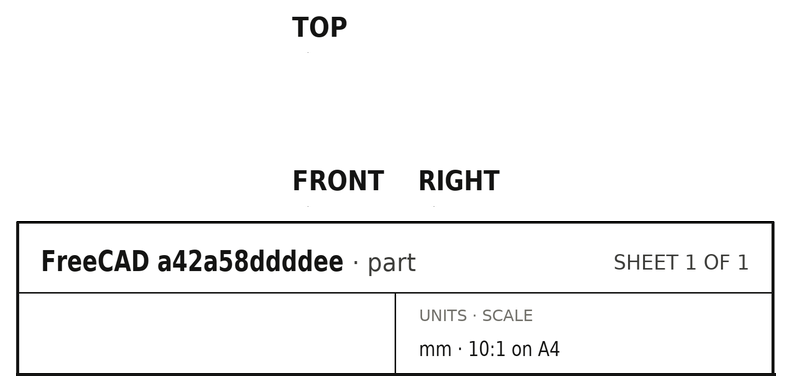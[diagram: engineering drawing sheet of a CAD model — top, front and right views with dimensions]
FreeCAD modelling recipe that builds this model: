
FCSTD DOCUMENT  (FreeCAD 0.21R33694 (Git))
Label: diffPair
License: All rights reserved
LicenseURL: http://en.wikipedia.org/wiki/All_rights_reserved
objects: Part::Part2DObjectPython×23, App::FeaturePython×10, Part::Extrusion×5, Part::Cut×3, Part::FeaturePython×2
note: 33 computed .brp shape members not serialized (recipe doc carries the construction recipe); baked Part::Feature solids carry a one-line shape summary decoded from their .brp

FEATURE [Part::Part2DObjectPython] Wire  # Draft 2D object (typed FeaturePython)
  Area = 0.0014181
  ChamferSize = 0
  Closed = true
  End = (-0.05,0,0)
  FilletRadius = 0
  Length = 0.221006
  MakeFace = true
  Placement = pos=(-0.15,0,0) rot=(0,0,1;0rad)
  Points = (4) [(0,0,0),(0.00545955,0.015,0),(0.0945402,0.015,0),(0.1,-6.12323e-18,0)]
  Start = (-0.15,0,0)
  Subdivisions = 0
FEATURE [Part::Part2DObjectPython] Wire001  # Draft 2D object (typed FeaturePython)
  Area = 0.0014181
  ChamferSize = 0
  Closed = true
  End = (0.15,0,0)
  FilletRadius = 0
  Length = 0.221006
  MakeFace = true
  Placement = pos=(0.05,0,0) rot=(0,0,1;0rad)
  Points = (4) [(0,0,0),(0.00545955,0.015,0),(0.0945402,0.015,0),(0.1,-6.12323e-18,0)]
  Start = (0.05,0,0)
  Subdivisions = 0
FEATURE [Part::Part2DObjectPython] Rectangle  # Draft 2D object (typed FeaturePython)
  Area = 0.13
  ChamferSize = 0
  Columns = 1
  FilletRadius = 0
  Height = 0.1
  Length = 1.3
  MakeFace = true
  Placement = pos=(-0.65,-0.1,0) rot=(0,0,1;0rad)
  Rows = 1
FEATURE [Part::Part2DObjectPython] Rectangle001  # Draft 2D object (typed FeaturePython)
  Area = 0.13
  ChamferSize = 0
  Columns = 1
  FilletRadius = 0
  Height = 0.1
  Length = 1.3
  MakeFace = true
  Placement = pos=(-0.65,0,0) rot=(0,0,1;0rad)
  Rows = 1
FEATURE [Part::Part2DObjectPython] Clone2D  label="Wire (2D)"  # Draft 2D object (typed FeaturePython)
  Fuse = false
  Objects = -> [Wire]
  Placement = pos=(-0.15,0,0) rot=(0,0,1;0rad)
  Scale = (1,1,1)
FEATURE [Part::Part2DObjectPython] Clone2D001  label="Wire001 (2D)"  # Draft 2D object (typed FeaturePython)
  Fuse = false
  Objects = -> [Wire001]
  Placement = pos=(0.05,0,0) rot=(0,0,1;0rad)
  Scale = (1,1,1)
FEATURE [Part::Part2DObjectPython] Clone2D002  label="Rectangle (2D)"  # Draft 2D object (typed FeaturePython)
  Fuse = false
  Objects = -> [Rectangle]
  Placement = pos=(-0.65,-0.1,0) rot=(0,0,1;0rad)
  Scale = (1,1,1)
FEATURE [Part::Part2DObjectPython] Clone2D003  label="Rectangle001 (2D)"  # Draft 2D object (typed FeaturePython)
  Fuse = false
  Objects = -> [Rectangle001]
  Placement = pos=(-0.65,0,0) rot=(0,0,1;0rad)
  Scale = (1,1,1)
FEATURE [Part::Part2DObjectPython] Clone2D004  label="Wire (2D)001"  # Draft 2D object (typed FeaturePython)
  Fuse = false
  Objects = -> [Wire]
  Placement = pos=(-0.15,0,0) rot=(0,0,1;0rad)
  Scale = (1,1,1)
FEATURE [Part::Part2DObjectPython] Clone2D005  label="Wire001 (2D)001"  # Draft 2D object (typed FeaturePython)
  Fuse = false
  Objects = -> [Wire001]
  Placement = pos=(0.05,0,0) rot=(0,0,1;0rad)
  Scale = (1,1,1)
FEATURE [Part::Part2DObjectPython] Clone2D006  label="Rectangle (2D)001"  # Draft 2D object (typed FeaturePython)
  Fuse = false
  Objects = -> [Rectangle]
  Placement = pos=(-0.65,-0.1,0) rot=(0,0,1;0rad)
  Scale = (1,1,1)
FEATURE [Part::Part2DObjectPython] Clone2D007  label="Rectangle001 (2D)001"  # Draft 2D object (typed FeaturePython)
  Fuse = false
  Objects = -> [Rectangle001]
  Placement = pos=(-0.65,0,0) rot=(0,0,1;0rad)
  Scale = (1,1,1)
FEATURE [Part::Extrusion] Extrude004
  Base = -> Clone2D
  Dir = (0,0,1)
  DirMode = 2
  FaceMakerClass = Part::FaceMakerBullseye
  LengthFwd = 2
  LengthRev = 0
  Solid = false
  Symmetric = false
FEATURE [Part::Extrusion] Extrude005
  Base = -> Clone2D001
  Dir = (0,0,1)
  DirMode = 2
  FaceMakerClass = Part::FaceMakerBullseye
  LengthFwd = 2
  LengthRev = 0
  Solid = false
  Symmetric = false
FEATURE [Part::Extrusion] Extrude006
  Base = -> Clone2D002
  Dir = (0,0,1)
  DirMode = 2
  FaceMakerClass = Part::FaceMakerBullseye
  LengthFwd = 2
  LengthRev = 0
  Solid = false
  Symmetric = false
FEATURE [Part::Extrusion] Extrude007
  Base = -> Clone2D003
  Dir = (0,0,1)
  DirMode = 2
  FaceMakerClass = Part::FaceMakerBullseye
  LengthFwd = 2
  LengthRev = 0
  Solid = false
  Symmetric = false
FEATURE [Part::Cut] Cut002
  Base = -> Extrude007
  Tool = -> Extrude004
FEATURE [Part::Cut] Cut003
  Base = -> Cut002
  Tool = -> Extrude005
FEATURE [App::FeaturePython] Text010  label="_Sin(PV){port1}"  # WARN: FeaturePython — macro-defined, semantics opaque (R4)
  Placement = pos=(5.00075,-5.09743,10) rot=(0,0,1;0rad)
  Text = .
FEATURE [App::FeaturePython] Text011  label="_Sout(PV){port2}"  # WARN: FeaturePython — macro-defined, semantics opaque (R4)
  Placement = pos=(5.00075,-5.09743,10) rot=(0,0,1;0rad)
  Text = .
FEATURE [App::FeaturePython] Text012  label="_Lin(1,voltage,in1){v11}"  # WARN: FeaturePython — macro-defined, semantics opaque (R4)
  Placement = pos=(5.00075,-5.09743,10) rot=(0,0,1;0rad)
  Text = .
FEATURE [App::FeaturePython] Text013  label="_Lin(1,current,in1){i11}"  # WARN: FeaturePython — macro-defined, semantics opaque (R4)
  Placement = pos=(5.00075,-5.09743,10) rot=(0,0,1;0rad)
  Text = .
FEATURE [App::FeaturePython] Text014  label="_Lin(2,voltage,in2){v12}"  # WARN: FeaturePython — macro-defined, semantics opaque (R4)
  Placement = pos=(5.00075,-5.09743,10) rot=(0,0,1;0rad)
  Text = .
FEATURE [App::FeaturePython] Text015  label="_Lin(2,current,in2){i12}"  # WARN: FeaturePython — macro-defined, semantics opaque (R4)
  Placement = pos=(5.00075,-5.09743,10) rot=(0,0,1;0rad)
  Text = .
FEATURE [App::FeaturePython] Text016  label="_Lout(3,voltage,out3){v21}"  # WARN: FeaturePython — macro-defined, semantics opaque (R4)
  Placement = pos=(5.00075,-5.09743,10) rot=(0,0,1;0rad)
  Text = .
FEATURE [App::FeaturePython] Text017  label="_Lout(3,current,out3){i21}"  # WARN: FeaturePython — macro-defined, semantics opaque (R4)
  Placement = pos=(5.00075,-5.09743,10) rot=(0,0,1;0rad)
  Text = .
FEATURE [App::FeaturePython] Text018  label="_Lout(4,voltage,out4){v22}"  # WARN: FeaturePython — macro-defined, semantics opaque (R4)
  Placement = pos=(5.00075,-5.09743,10) rot=(0,0,1;0rad)
  Text = .
FEATURE [App::FeaturePython] Text019  label="_Lout(4,current,out4){i22}"  # WARN: FeaturePython — macro-defined, semantics opaque (R4)
  Placement = pos=(5.00075,-5.09743,10) rot=(0,0,1;0rad)
  Text = .
FEATURE [Part::Part2DObjectPython] Wire006  label="_Pi22"  # Draft 2D object (typed FeaturePython)
  Area = 1.4181e-09
  ChamferSize = 0
  Closed = true
  End = (5e-05,-0.0999,4.995)
  FilletRadius = 0
  Length = 0.000221006
  MakeFace = true
  Placement = pos=(0.00015,-0.0999,4.995) rot=(0.707107,0.707107,0;3.14159rad)
  Points = (4) [(0,0,0),(1.5e-05,-5.45983e-06,0),(1.5e-05,-9.45404e-05,0),(0,-0.0001,0)]
  Start = (0.00015,-0.0999,4.995)
  Subdivisions = 0
FEATURE [Part::Part2DObjectPython] Wire007  label="_Pi21"  # Draft 2D object (typed FeaturePython)
  Area = 1.4181e-09
  ChamferSize = 0
  Closed = true
  End = (-0.00015,-0.0999,4.995)
  FilletRadius = 0
  Length = 0.000221006
  MakeFace = true
  Placement = pos=(-5e-05,-0.0999,4.995) rot=(0.707107,0.707107,0;3.14159rad)
  Points = (4) [(0,0,0),(1.5e-05,-5.45983e-06,0),(1.5e-05,-9.45404e-05,0),(0,-0.0001,0)]
  Start = (-5e-05,-0.0999,4.995)
  Subdivisions = 0
FEATURE [Part::Part2DObjectPython] Wire008  label="_Pi11"  # Draft 2D object (typed FeaturePython)
  Area = 1.4181e-09
  ChamferSize = 0
  Closed = true
  End = (-5e-05,-0.0999,4.997)
  FilletRadius = 0
  Length = 0.000221006
  MakeFace = true
  Placement = pos=(-0.00015,-0.0999,4.997) rot=(0,0,1;0rad)
  Points = (4) [(0,0,0),(5.45955e-06,1.5e-05,0),(9.45402e-05,1.5e-05,0),(0.0001,0,0)]
  Start = (-0.00015,-0.0999,4.997)
  Subdivisions = 0
FEATURE [Part::Part2DObjectPython] Wire009  label="_Pi12"  # Draft 2D object (typed FeaturePython)
  Area = 1.4181e-09
  ChamferSize = 0
  Closed = true
  End = (0.00015,-0.0999,4.997)
  FilletRadius = 0
  Length = 0.000221006
  MakeFace = true
  Placement = pos=(5e-05,-0.0999,4.997) rot=(0,0,1;0rad)
  Points = (4) [(0,0,0),(5.45955e-06,1.5e-05,0),(9.45402e-05,1.5e-05,0),(0.0001,0,0)]
  Start = (5e-05,-0.0999,4.997)
  Subdivisions = 0
FEATURE [Part::Part2DObjectPython] Rectangle013  label="_Pport1"  # Draft 2D object (typed FeaturePython)
  Area = 2.6e-07
  ChamferSize = 0
  Columns = 1
  FilletRadius = 0
  Height = 0.0002
  Length = 0.0013
  MakeFace = true
  Placement = pos=(-0.00065,-0.1,4.997) rot=(0,0,1;0rad)
  Rows = 1
FEATURE [Part::Part2DObjectPython] Line  label="_Pv11"  # Draft 2D object (typed FeaturePython)
  Area = 0
  ChamferSize = 0
  Closed = false
  End = (-0.0001,-0.0999,4.997)
  FilletRadius = 0
  Length = 0.0001
  MakeFace = true
  Placement = pos=(0,-0.1,4.997) rot=(0,0,1;0rad)
  Points = (2) [(-0.0001,0,0),(-0.0001,0.0001,0)]
  Start = (-0.0001,-0.1,4.997)
  Subdivisions = 0
FEATURE [Part::Part2DObjectPython] Line004  label="_Pv12"  # Draft 2D object (typed FeaturePython)
  Area = 0
  ChamferSize = 0
  Closed = false
  End = (0.0001,-0.0999,4.997)
  FilletRadius = 0
  Length = 0.0001
  MakeFace = true
  Placement = pos=(0,-0.1,4.997) rot=(0,0,1;0rad)
  Points = (2) [(0.0001,0,0),(0.0001,0.0001,0)]
  Start = (0.0001,-0.1,4.997)
  Subdivisions = 0
FEATURE [Part::Part2DObjectPython] Rectangle014  label="_Pport2"  # Draft 2D object (typed FeaturePython)
  Area = 2.6e-07
  ChamferSize = 0
  Columns = 1
  FilletRadius = 0
  Height = 0.0013
  Length = 0.0002
  MakeFace = true
  Placement = pos=(-0.00065,-0.1,4.995) rot=(0.707107,0.707107,0;3.14159rad)
  Rows = 1
FEATURE [Part::Part2DObjectPython] Line005  label="_Pv21"  # Draft 2D object (typed FeaturePython)
  Area = 0
  ChamferSize = 0
  Closed = false
  End = (-0.0001,-0.0999,4.995)
  FilletRadius = 0
  Length = 0.0001
  MakeFace = true
  Placement = pos=(0,-0.1,4.995) rot=(0.707107,0.707107,0;3.14159rad)
  Points = (2) [(1.38778e-17,-0.0001,0),(0.0001,-0.0001,0)]
  Start = (-0.0001,-0.1,4.995)
  Subdivisions = 0
FEATURE [Part::Part2DObjectPython] Line006  label="_Pv22"  # Draft 2D object (typed FeaturePython)
  Area = 0
  ChamferSize = 0
  Closed = false
  End = (0.0001,-0.0999,4.995)
  FilletRadius = 0
  Length = 0.0001
  MakeFace = true
  Placement = pos=(0,-0.1,4.995) rot=(0.707107,0.707107,0;3.14159rad)
  Points = (2) [(1.38778e-17,0.0001,0),(0.0001,0.0001,0)]
  Start = (0.0001,-0.1,4.995)
  Subdivisions = 0
FEATURE [Part::Part2DObjectPython] Rectangle015  # Draft 2D object (typed FeaturePython)
  Area = 0.01
  ChamferSize = 0
  Columns = 1
  FilletRadius = 0
  Height = 0.1
  Length = 0.1
  MakeFace = true
  Placement = pos=(-0.15,0,2.45) rot=(1,0,0;1.5708rad)
  Rows = 1
FEATURE [Part::Extrusion] Extrude
  Base = -> Rectangle015
  Dir = (0,-1,2e-16)
  DirMode = 2
  FaceMakerClass = Part::FaceMakerBullseye
  LengthFwd = 0.1
  LengthRev = 0
  Placement = pos=(0,0,-1.5) rot=(0,0,1;0rad)
  Solid = false
  Symmetric = false
FEATURE [Part::Cut] Cut
  Base = -> Extrude006
  Tool = -> Extrude
FEATURE [Part::FeaturePython] BooleanFragments  # WARN: FeaturePython — macro-defined, semantics opaque (R4)
  Mode = 0
  Objects = -> [Cut003,Cut]
  Tolerance = 0
FEATURE [Part::FeaturePython] Clone  label="scaled"  # Draft clone (typed FeaturePython)
  AttacherType = Attacher::AttachEngine3D
  Fuse = false
  Objects = -> [BooleanFragments]
  Placement = pos=(0,-0.0999,4.995) rot=(0,0,1;0rad)
  Scale = (0.001,0.001,0.001)
